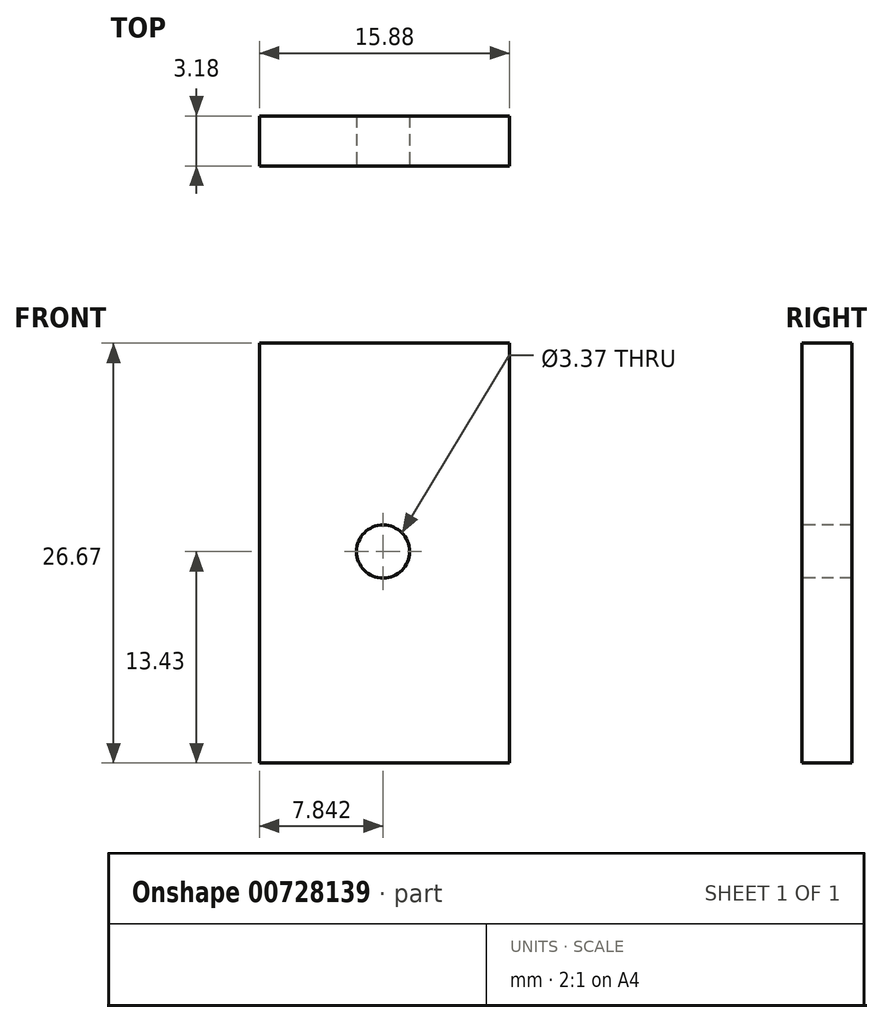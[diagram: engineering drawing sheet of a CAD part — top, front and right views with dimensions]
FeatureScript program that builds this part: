
annotation { "Feature Type Name" : "Feature", "Feature Type Description" : "" }
export const myFeature = defineFeature(function(context is Context, id is Id, definition is map)
    precondition{}
    {
        {
            var Q0;
            Q0=qCreatedBy(makeId("Front.planeOp"),FACE);
            var sketch = newSketch(context, id + "F0", { "sketchPlane" : qUnion([Q0])});
            skLineSegment(sketch, "E0.bottom", {"start": v(9.52, 38.1) * mm, "end": v(-9.53, 38.1) * mm});
            skLineSegment(sketch, "E0.top", {"start": v(9.53, -38.1) * mm, "end": v(-9.52, -38.1) * mm});
            skLineSegment(sketch, "E0.left", {"start": v(9.52, 38.1) * mm, "end": v(9.53, -38.1) * mm});
            skLineSegment(sketch, "E0.right", {"start": v(-9.53, 38.1) * mm, "end": v(-9.52, -38.1) * mm});
            skPoint(sketch, "E0.middle", {"position": v(0, 0) * mm});
            skLineSegment(sketch, "E1", {"start": v(-6.35, 38.1) * mm, "end": v(-6.35, -38.1) * mm});
            skLineSegment(sketch, "E2", {"start": v(-9.53, 29.2) * mm, "end": v(-6.35, 29.2) * mm});
            skLineSegment(sketch, "E3", {"start": v(-9.53, 20.32) * mm, "end": v(-6.35, 20.32) * mm});
            skLineSegment(sketch, "E4", {"start": v(-9.53, 11.43) * mm, "end": v(-6.35, 11.43) * mm});
            skLineSegment(sketch, "E5", {"start": v(-9.53, -1.27) * mm, "end": v(-6.35, -1.27) * mm});
            skLineSegment(sketch, "E6", {"start": v(-9.52, -13.97) * mm, "end": v(-6.35, -13.97) * mm});
            skLineSegment(sketch, "E7", {"start": v(-6.35, 11.43) * mm, "end": v(9.53, 11.43) * mm});
            skSolve(sketch);
        }
        {
            var Q0;
            {var subQ5=sQuery(id+"F0.wireOp",EDGE,"QXyYzKvK-Vf3k-rWq0-lT2y-zqTFrBfQWzn5");Q0=makeQuery(id+"F0.imprint","IMPRINT",FACE,{"disambiguationData":[TD([[makeQuery(id+"F0.imprint","IMPRINT",EDGE,{"derivedFrom":subQ5}),1.0]])]});}
            var Q1;
            {var subQ5=sQuery(id+"F0.wireOp",EDGE,"E7");Q1=makeQuery(id+"F0.imprint","IMPRINT",FACE,{"disambiguationData":[TD([[makeQuery(id+"F0.imprint","IMPRINT",EDGE,{"derivedFrom":subQ5}),1.0]])]});}
            extrude(context, id + "F1", {"entities" : qUnion([Q0, Q1]), "depth" : 3.17 * mm, "offsetDistance" : 25.4 * mm});
        }
        {
            var Q0;
            Q0=makeQuery(id+"F1.opExtrude","CAP_FACE",FACE,{"disambiguationData":[OSD([sQuery(id+"F0.wireOp",EDGE,"E0.bottom"),sQuery(id+"F0.wireOp",EDGE,"E0.top"),sQuery(id+"F0.wireOp",EDGE,"E0.left"),sQuery(id+"F0.wireOp",EDGE,"E0.right"),sQuery(id+"F0.wireOp",EDGE,"E1"),sQuery(id+"F0.wireOp",EDGE,"E2"),sQuery(id+"F0.wireOp",EDGE,"E3"),sQuery(id+"F0.wireOp",EDGE,"E4"),sQuery(id+"F0.wireOp",EDGE,"E5"),sQuery(id+"F0.wireOp",EDGE,"E6")])],"isStart":false});
            var sketch = newSketch(context, id + "F2", { "sketchPlane" : qUnion([Q0])});
            skCircle(sketch, "E8", {"center": v(1.5, 24.86) * mm, "radius": 1.68 * mm});
            skSolve(sketch);
        }
        {
            var Q0;
            Q0=qSketchRegion(id+"F2",true);
            extrude(context, id + "F3", {"entities" : qUnion([Q0]), "operationType" : NewBodyOperationType.REMOVE, "endBound" : BoundingType.THROUGH_ALL, "oppositeDirection" : true, "depth" : 25.4 * mm, "offsetDistance" : 25.4 * mm});
        }
    });
